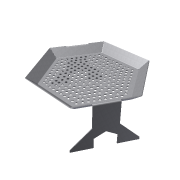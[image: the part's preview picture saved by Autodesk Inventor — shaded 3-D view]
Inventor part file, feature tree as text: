
AUTODESK INVENTOR PART (.ipt)
format: ipt  version: 2012 (Build 160160000, 160)  size: 1,092,608 bytes
history: native  units: mm
features: sheet_metal_op x18, sketch x12, other x11, mirror x2, plane x2, hole x1, projected_geometry x1
ambient origin geometry x8: Origin, YZ Plane, XZ Plane, XY Plane, X Axis, Y Axis, Z Axis, Center Point
bodies: Solid1 (feature_tree)
feature tree (47):
  sheet_metal_op  "Face1"
  sheet_metal_op  "Flange1"
  sketch  "Sketch3"  dims[d4=0.75mm]
  sheet_metal_op  "Flange4"
  sheet_metal_op  "Flange5"
  hole  "Hole1"  [1 undecoded]
  mirror  "Mirror1"
  sheet_metal_op  "Face2"
  plane  "Work Plane1"
  sheet_metal_op  "Face5"
  sheet_metal_op  "Face4"
  sheet_metal_op  "Bend10"
  plane  "Work Plane2"
  mirror  "Mirror3"
  sheet_metal_op  "Bend11"
  sketch  "Sketch1"  dims[d1=200.0mm d2=1.5mm]
  other  "Plate1"
  sketch  "Sketch2"  dims[d3=1.5mm]
  other  "Plate2"
  sheet_metal_op  "Bend1"
  sheet_metal_op  "Corner1"
  sketch  "Sketch7"  dims[d5=3.0mm]
  other  "Plate5"
  sheet_metal_op  "Bend4"
  sheet_metal_op  "Corner4"
  sketch  "Sketch8"  dims[d6=1.5mm]
  other  "Plate6"
  sheet_metal_op  "Bend5"
  sheet_metal_op  "Corner5"
  sketch  "Sketch14"  dims[d7=25.0mm d8=45.0deg d9=1.5mm]
  other  "Plate8"
  sheet_metal_op  "Bend7"
  sketch  "Sketch15"  dims[d10=6.0mm]
  sketch  "Sketch18"  dims[d11=1.5mm]
  sketch  "Sketch19"  dims[d12=1.5mm]
  other  "Plate10"
  sheet_metal_op  "Bend9"
  sketch  "Sketch21"  dims[d22=70.0mm]
  projected_geometry  "Projected Loop3"
  other  "Plate11"
  sheet_metal_op  "Bend12"
  sketch  "Sketch22"  dims[d23=5.0mm d24=5.0mm d25=5.0mm d26=5.0mm d27=5.0mm d28=5.0mm d29=90.0mm d31=10.0mm d32=10.0mm d34=10.0mm d36=90.0mm d38=10.0mm d39=10.0mm d41=10.0mm d43=80.0mm d45=10.0mm d46=10.0mm d48=10.0mm d50=170.0mm d52=10.0mm d53=10.0mm d55=10.0mm d108=1.5mm d109=0.75mm d110=3.0mm d111=1.5mm d112=35.0mm d113=35.0mm d114=100.0mm d115=135.0deg d116=1.5mm d117=6.0mm d118=1.5mm d119=1.5mm d120=1.5mm d121=0.75mm d122=3.0mm d123=1.5mm d124=35.0mm d125=35.0mm d126=100.0mm d127=135.0deg d128=1.5mm d129=6.0mm d130=1.5mm d131=1.5mm d143=2.0mm d144=2.0mm d145=2.0mm d146=0.5mm d147=2.0mm d148=0.5mm d149=2.0mm d150=0.5mm d151=2.0mm d152=0.5mm d153=70.0mm d155=9.5mm d156=10.0mm d158=10.0mm d160=140.0mm d162=10.35mm d163=10.0mm d165=10.0mm d167=80.0mm d169=10.0mm d170=10.0mm d172=10.0mm d174=60.0mm d176=10.0mm d177=10.0mm d179=10.0mm d209=40.0mm d211=11.5mm d212=10.0mm d214=10.0mm d216=70.0mm d218=9.5mm d219=10.0mm d221=10.0mm d223=40.0mm d225=9.0mm d226=10.0mm d228=10.0mm d230=100.0mm d232=10.0mm d233=10.0mm d235=10.0mm d265=20.0mm d267=11.5mm d268=10.0mm d270=10.0mm d272=50.0mm d274=11.0mm d275=10.0mm d277=10.0mm d279=60.0mm d281=11.0mm d282=10.0mm d284=10.0mm d286=5.5mm d287=6.0mm d288=4.0mm d289=2.0mm d290=90.0deg d291=1.5mm d292=20.594885mm d328=1.5mm d329=1.5mm d330=0.75mm d331=3.0mm d332=1.5mm d334=5.0mm d335=5.0mm d336=40.0mm d337=40.0mm d338=10.0mm d339=50.0mm d340=1.5mm d341=0.0mm d349=30.0mm d350=30.0mm d351=1.5mm d352=0.0mm d353=20.0mm d354=1.5mm d355=1.5mm d356=0.75mm d357=3.0mm d358=1.5mm d359=1.5mm d360=0.75mm d361=3.0mm d362=1.5mm d363=1.5mm d364=1.5mm d365=0.75mm d366=3.0mm d367=1.5mm d368=1.5mm d369=1.5mm d370=1.5mm d371=0.75mm d372=3.0mm d373=1.5mm d374=1.5mm d375=0.0mm]
  other  "Cut6"
  other  "Cut9"
  other  "Cut8"
  sketch  "Sketch20"  dims[d14=0.5mm d16=0.5mm]
  other  "Definition1"
note: 1 required parameter value undecoded (feature->parameter linkage not recoverable at this tier; creation-order binding heuristic only, values carry confidence <= 0.55)
